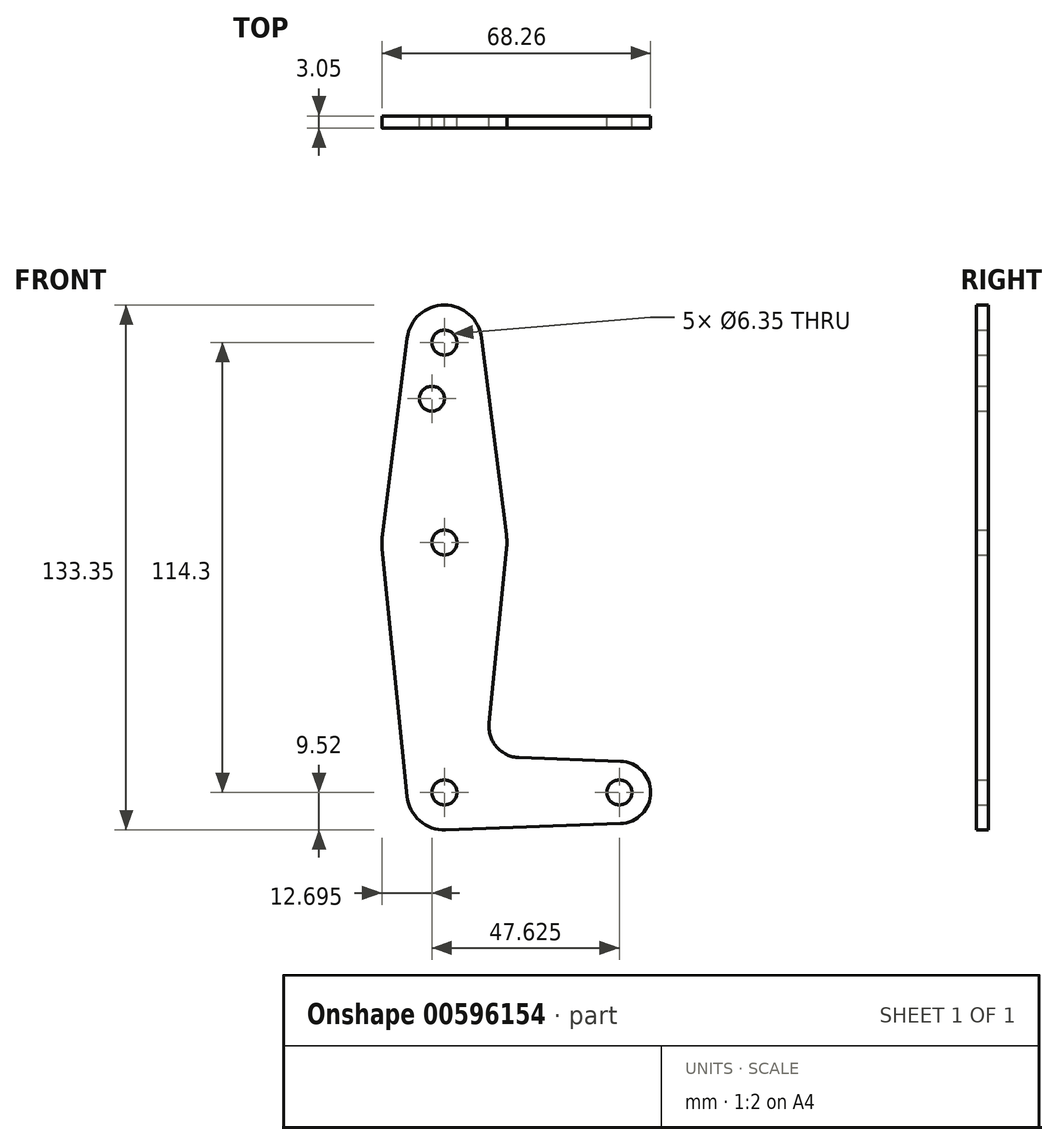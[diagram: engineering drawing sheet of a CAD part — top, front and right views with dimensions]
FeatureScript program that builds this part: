
annotation { "Feature Type Name" : "Feature", "Feature Type Description" : "" }
export const myFeature = defineFeature(function(context is Context, id is Id, definition is map)
    precondition{}
    {
        {
            var Q0;
            Q0=qCreatedBy(makeId("Front.planeOp"),FACE);
            var sketch = newSketch(context, id + "F0", { "sketchPlane" : qUnion([Q0])});
            skLineSegment(sketch, "E0", {"start": v(0, -42.7) * mm, "end": v(0, 135.52) * mm, "construction": true});
            skLineSegment(sketch, "E1", {"start": v(-38.24, 0) * mm, "end": v(59.02, 0) * mm, "construction": true});
            skCircle(sketch, "E2", {"center": v(0, 0) * mm, "radius": 9.53 * mm});
            skCircle(sketch, "E3", {"center": v(0, 63.5) * mm, "radius": 15.88 * mm});
            skCircle(sketch, "E4", {"center": v(0, 114.3) * mm, "radius": 9.53 * mm});
            skCircle(sketch, "E5", {"center": v(44.45, 0) * mm, "radius": 7.94 * mm});
            skCircle(sketch, "E6", {"center": v(0, 114.3) * mm, "radius": 3.18 * mm});
            skCircle(sketch, "E7", {"center": v(0, 63.5) * mm, "radius": 3.18 * mm});
            skCircle(sketch, "E8", {"center": v(0, 0) * mm, "radius": 3.18 * mm});
            skCircle(sketch, "E9", {"center": v(44.45, 0) * mm, "radius": 3.18 * mm});
            skCircle(sketch, "E10", {"center": v(-3.18, 100.03) * mm, "radius": 3.18 * mm});
            skLineSegment(sketch, "E11", {"start": v(-15.75, 65.48) * mm, "end": v(-9.45, 115.5) * mm});
            skLineSegment(sketch, "E12", {"start": v(15.75, 65.48) * mm, "end": v(9.45, 115.5) * mm});
            skPoint(sketch, "E13.newPointB", {"position": v(0, 7.94) * mm});
            skLineSegment(sketch, "E14", {"start": v(-15.8, 61.91) * mm, "end": v(-9.48, -0.95) * mm});
            skLineSegment(sketch, "E15", {"start": v(18.97, 8.85) * mm, "end": v(44.73, 7.93) * mm});
            skLineSegment(sketch, "E16", {"start": v(15.8, 61.91) * mm, "end": v(11.34, 17.6) * mm});
            skLineSegment(sketch, "E17", {"start": v(0.34, -9.52) * mm, "end": v(44.73, -7.93) * mm});
            skArc(sketch, "E18.filletArc", {"start": v(11.34, 17.6) * mm, "mid": v(13.26, 11.57) * mm, "end": v(18.97, 8.85) * mm});
            skSolve(sketch);
        }
        {
            var Q0;
            Q0 = qSketchRegion(id + "F0", true);
            extrude(context, id + "F1", {"entities" : qUnion([Q0]), "depth" : 3.05 * mm, "offsetDistance" : 25.4 * mm});
        }
    });
